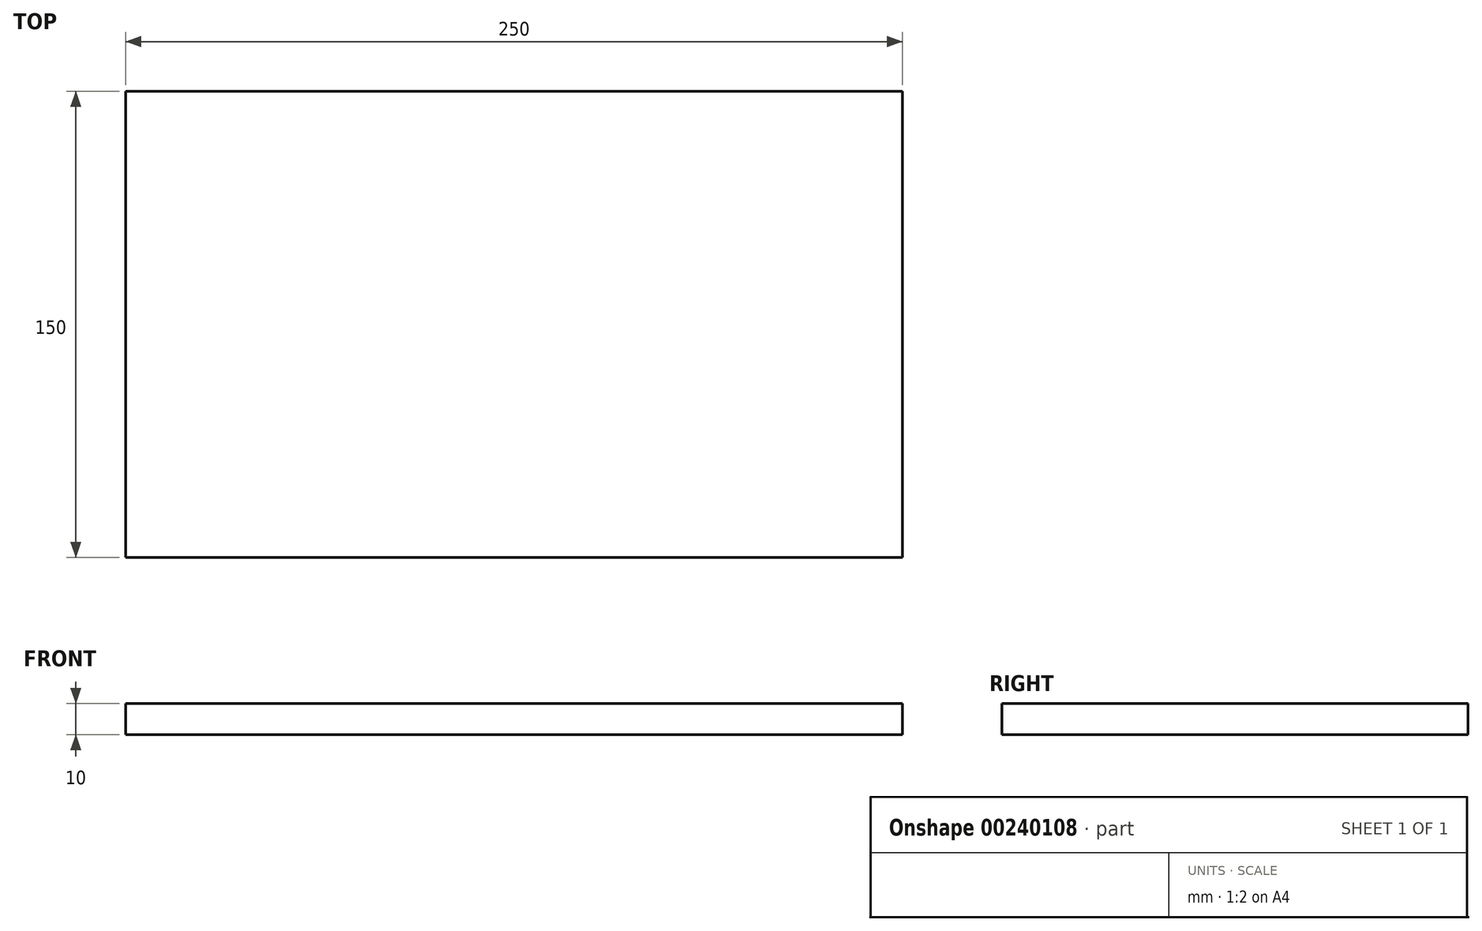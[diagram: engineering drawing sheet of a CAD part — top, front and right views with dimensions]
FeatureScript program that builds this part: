
annotation { "Feature Type Name" : "Feature", "Feature Type Description" : "" }
export const myFeature = defineFeature(function(context is Context, id is Id, definition is map)
    precondition{}
    {
        {
            var Q0;
            Q0=qCreatedBy(makeId("Top.planeOp"),FACE);
            var sketch = newSketch(context, id + "F0", { "sketchPlane" : qUnion([Q0])});
            skLineSegment(sketch, "E0.bottom", {"start": v(125, -75) * mm, "end": v(-125, -75) * mm});
            skLineSegment(sketch, "E0.top", {"start": v(125, 75) * mm, "end": v(-125, 75) * mm});
            skLineSegment(sketch, "E0.left", {"start": v(125, -75) * mm, "end": v(125, 75) * mm});
            skLineSegment(sketch, "E0.right", {"start": v(-125, -75) * mm, "end": v(-125, 75) * mm});
            skPoint(sketch, "E0.middle", {"position": v(0, 0) * mm});
            skSolve(sketch);
        }
        {
            var Q0;
            Q0=makeQuery(id+"F0.imprint","IMPRINT",FACE,{"disambiguationData":[TD([[makeQuery(id+"F0.imprint","IMPRINT",EDGE,{"derivedFrom":sQuery(id+"F0.wireOp",EDGE,"E0.bottom")}),-1.0]])]});
            extrude(context, id + "F1", {"entities" : qUnion([Q0]), "depth" : 10 * mm});
        }
    });
